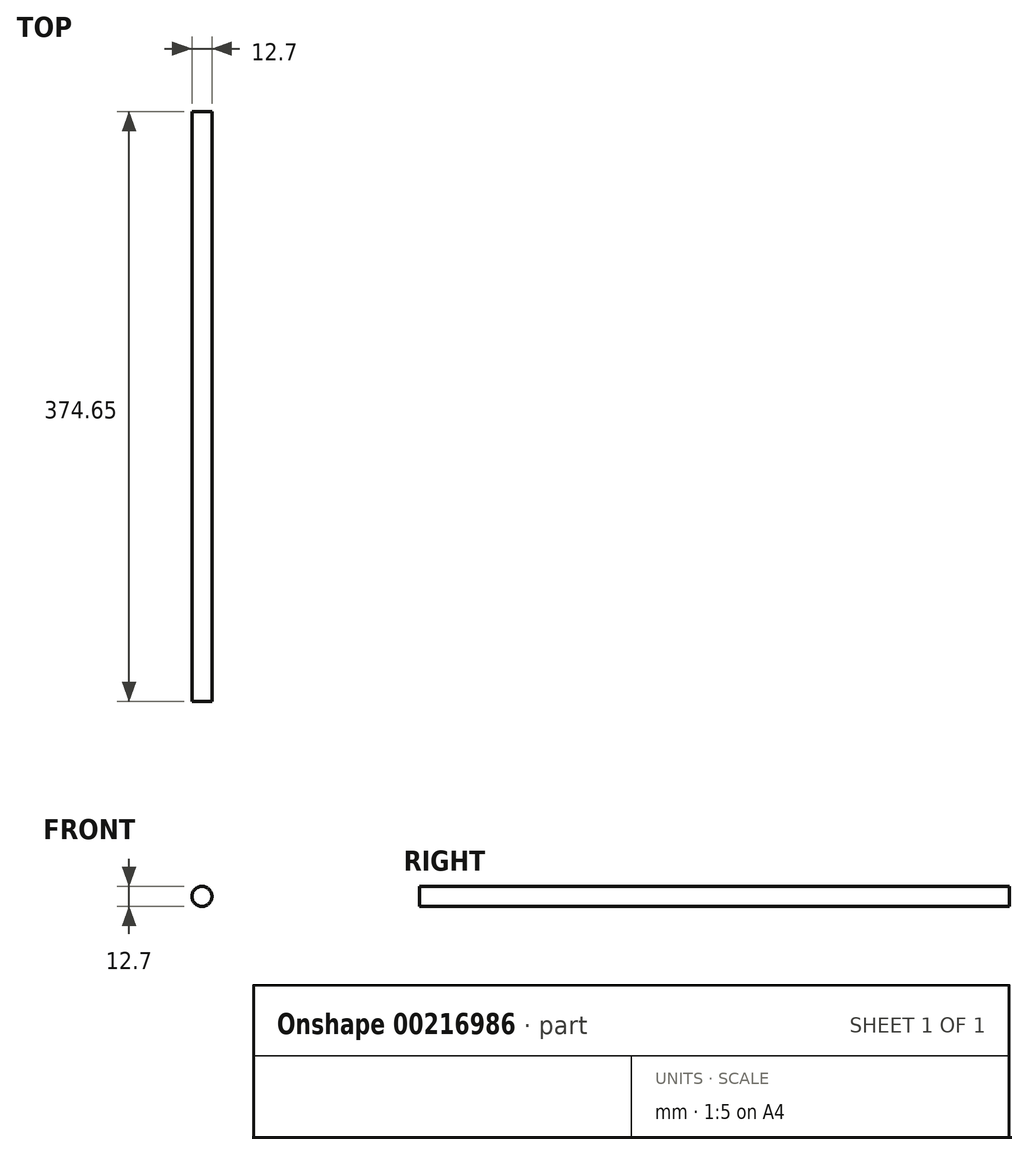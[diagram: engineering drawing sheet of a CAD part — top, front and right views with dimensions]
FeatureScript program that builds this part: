
annotation { "Feature Type Name" : "Feature", "Feature Type Description" : "" }
export const myFeature = defineFeature(function(context is Context, id is Id, definition is map)
    precondition{}
    {
        {
            var Q0;
            Q0=qCreatedBy(makeId("Front.planeOp"),FACE);
            var sketch = newSketch(context, id + "F0", { "sketchPlane" : qUnion([Q0])});
            skCircle(sketch, "E0", {"center": v(0, 0) * mm, "radius": 6.35 * mm});
            skSolve(sketch);
        }
        {
            var Q0;
            Q0=makeQuery(id+"F0.imprint","IMPRINT",FACE,{"disambiguationData":[TD([[makeQuery(id+"F0.imprint","IMPRINT",EDGE,{"derivedFrom":sQuery(id+"F0.wireOp",EDGE,"E0")}),1.0]])]});
            extrude(context, id + "F1", {"entities" : qUnion([Q0]), "depth" : 374.65 * mm});
        }
    });
